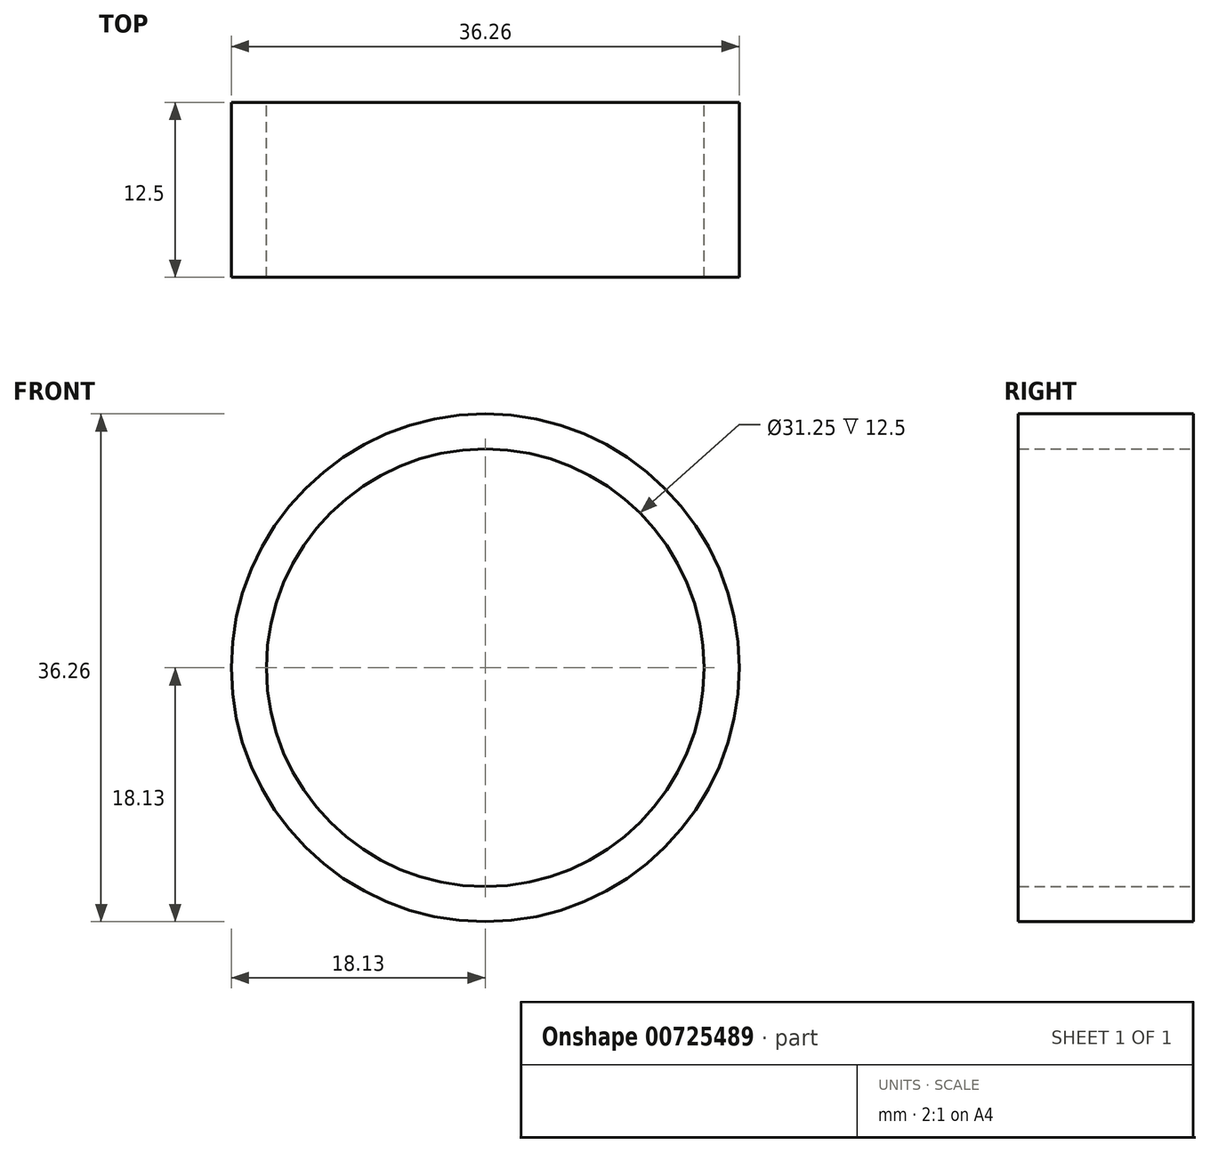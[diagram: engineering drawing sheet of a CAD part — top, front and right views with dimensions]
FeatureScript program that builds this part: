
annotation { "Feature Type Name" : "Feature", "Feature Type Description" : "" }
export const myFeature = defineFeature(function(context is Context, id is Id, definition is map)
    precondition{}
    {
        {
            var Q0;
            Q0=qCreatedBy(makeId("Front.planeOp"),FACE);
            var sketch = newSketch(context, id + "F0", { "sketchPlane" : qUnion([Q0])});
            skCircle(sketch, "E0", {"center": v(0, 0) * mm, "radius": 62.5 * mm});
            skCircle(sketch, "E1.0", {"center": v(0, 0) * mm, "radius": 72.5 * mm});
            skSolve(sketch);
        }
        {
            var Q0;
            Q0=makeQuery(id+"F0.imprint","IMPRINT",FACE,{"disambiguationData":[TD([[makeQuery(id+"F0.imprint","IMPRINT",EDGE,{"derivedFrom":sQuery(id+"F0.wireOp",EDGE,"E0")}),-1.0]])]});
            extrude(context, id + "F1", {"entities" : qUnion([Q0]), "depth" : 50 * mm, "offsetDistance" : 25 * mm});
        }
        {
            var Q0;
            Q0=makeQuery(id+"F1.opExtrude","SWEPT_BODY",BODY,{"disambiguationData":[OSD([sQuery(id+"F0.wireOp",EDGE,"E0"),sQuery(id+"F0.wireOp",EDGE,"E1.0")])]});
            var Q1;
            Q1=qCreatedBy(makeId("Right.planeOp"),FACE);
            var Q2;
            Q2=qCreatedBy(makeId("Origin.pointOp"),VERTEX);
            transform(context, id + "F2", {"entities" : qUnion([Q0]), "transformType" : TransformType.SCALE_UNIFORMLY, "scale" : .25, "scalePoint" : qUnion([Q2]), "makeCopy" : false});
        }
    });
